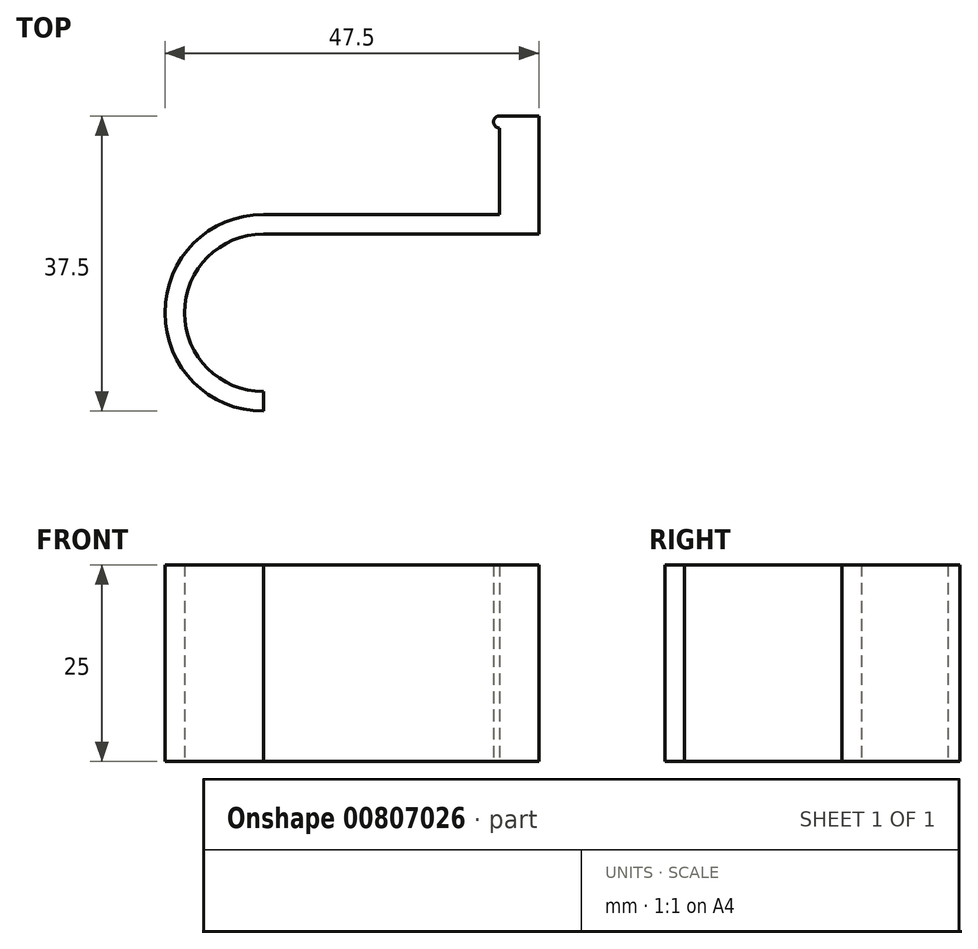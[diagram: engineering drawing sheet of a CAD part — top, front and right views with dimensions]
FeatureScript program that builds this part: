
annotation { "Feature Type Name" : "Feature", "Feature Type Description" : "" }
export const myFeature = defineFeature(function(context is Context, id is Id, definition is map)
    precondition{}
    {
        {
            var Q0;
            Q0=qCreatedBy(makeId("Top.planeOp"),FACE);
            var sketch = newSketch(context, id + "F0", { "sketchPlane" : qUnion([Q0])});
            skArc(sketch, "E0", {"start": v(0, 10) * mm, "mid": v(-10, 0) * mm, "end": v(0, -10) * mm});
            skArc(sketch, "E1", {"start": v(0, 12.5) * mm, "mid": v(-12.5, 0) * mm, "end": v(0, -12.5) * mm});
            skLineSegment(sketch, "E2", {"start": v(0, 12.5) * mm, "end": v(0, 10) * mm});
            skLineSegment(sketch, "E3", {"start": v(0, -10) * mm, "end": v(0, -12.5) * mm});
            skLineSegment(sketch, "E4.bottom", {"start": v(0, 12.5) * mm, "end": v(0, 12.5) * mm});
            skLineSegment(sketch, "E4.top", {"start": v(0, 10) * mm, "end": v(0, 10) * mm});
            skLineSegment(sketch, "E5.bottom", {"start": v(30, 10) * mm, "end": v(0, 10) * mm});
            skLineSegment(sketch, "E5.top", {"start": v(30, 12.5) * mm, "end": v(0, 12.5) * mm});
            skLineSegment(sketch, "E6.bottom", {"start": v(30, 10) * mm, "end": v(35, 10) * mm});
            skLineSegment(sketch, "E6.top", {"start": v(30, 25) * mm, "end": v(35, 25) * mm});
            skLineSegment(sketch, "E6.left", {"start": v(30, 12.5) * mm, "end": v(30, 23.48) * mm});
            skLineSegment(sketch, "E6.right", {"start": v(35, 10) * mm, "end": v(35, 25) * mm});
            skArc(sketch, "E7", {"start": v(30, 25) * mm, "mid": v(29.24, 24.24) * mm, "end": v(30, 23.48) * mm});
            skSolve(sketch);
        }
        {
            var Q0;
            Q0=makeQuery(id+"F0.imprint","IMPRINT",FACE,{"disambiguationData":[TD([[makeQuery(id+"F0.imprint","IMPRINT",EDGE,{"derivedFrom":sQuery(id+"F0.wireOp",EDGE,"E0")}),-1.0]])]});
            var Q1;
            Q1=makeQuery(id+"F0.imprint","IMPRINT",FACE,{"disambiguationData":[TD([[makeQuery(id+"F0.imprint","IMPRINT",EDGE,{"derivedFrom":sQuery(id+"F0.wireOp",EDGE,"E2")}),1.0]])]});
            extrude(context, id + "F1", {"entities" : qUnion([Q0, Q1]), "depth" : 25 * mm, "offsetDistance" : 25 * mm});
        }
    });
